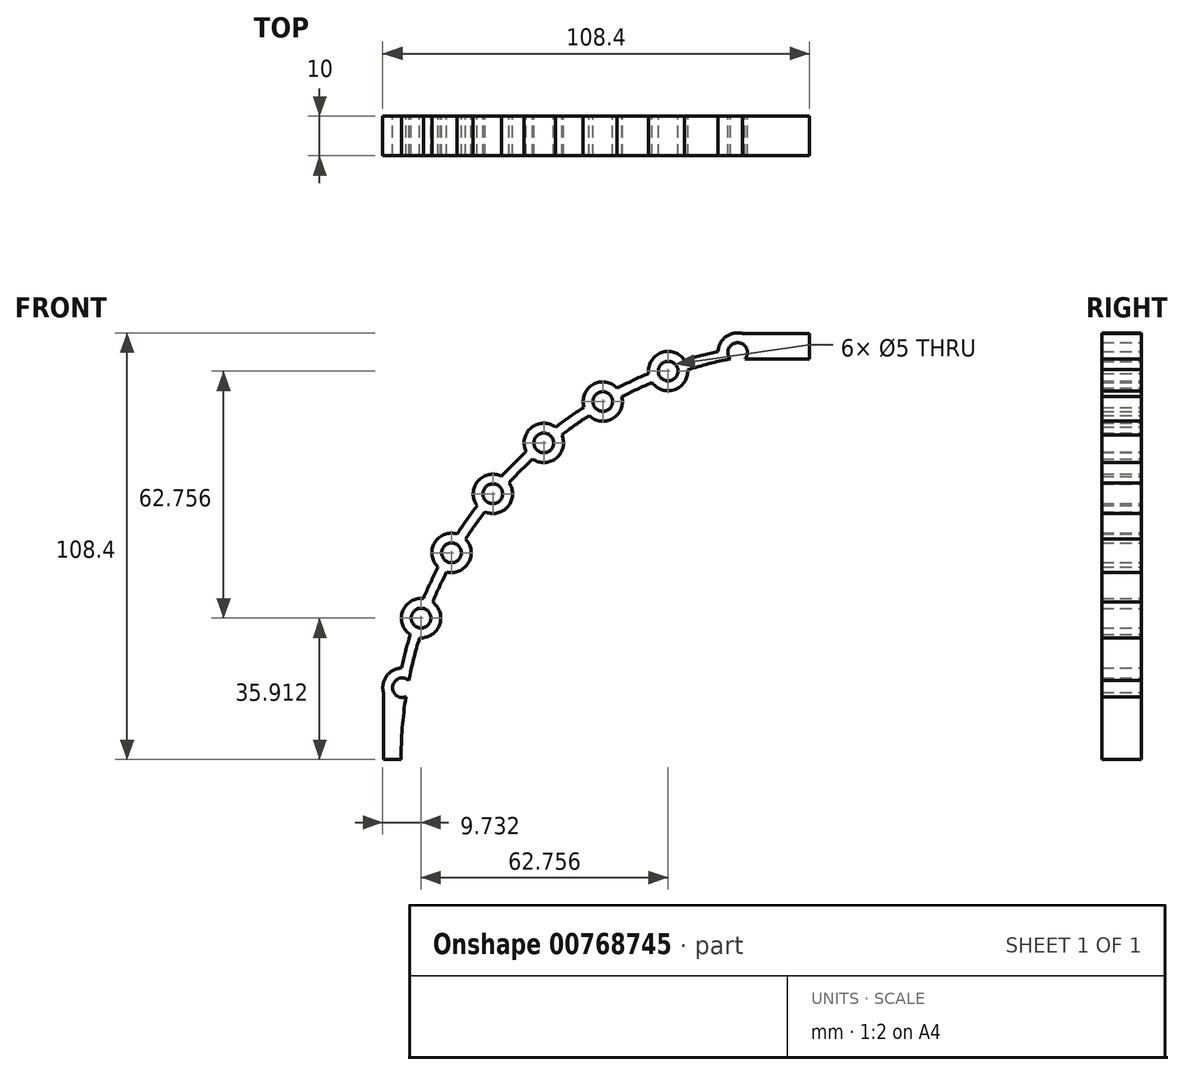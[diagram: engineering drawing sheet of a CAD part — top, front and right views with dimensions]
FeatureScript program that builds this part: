
annotation { "Feature Type Name" : "Feature", "Feature Type Description" : "" }
export const myFeature = defineFeature(function(context is Context, id is Id, definition is map)
    precondition{}
    {
        {
            var Q0;
            Q0=qCreatedBy(makeId("Front.planeOp"),FACE);
            var sketch = newSketch(context, id + "F0", { "sketchPlane" : qUnion([Q0])});
            skCircle(sketch, "E0", {"center": v(0, 0) * mm, "radius": 105 * mm, "construction": true});
            skLineSegment(sketch, "E1", {"start": v(0, 0) * mm, "end": v(0, 105) * mm, "construction": true});
            skLineSegment(sketch, "E2", {"start": v(0, 0) * mm, "end": v(0, -105) * mm, "construction": true});
            skLineSegment(sketch, "E3", {"start": v(0, 0) * mm, "end": v(-105, 0) * mm, "construction": true});
            skLineSegment(sketch, "E4", {"start": v(0, 0) * mm, "end": v(105, 0) * mm, "construction": true});
            skLineSegment(sketch, "E5", {"start": v(0, 0) * mm, "end": v(-18.23, 103.4) * mm, "construction": true});
            skLineSegment(sketch, "E6", {"start": v(0, 0) * mm, "end": v(-35.91, 98.67) * mm, "construction": true});
            skLineSegment(sketch, "E7", {"start": v(0, 0) * mm, "end": v(-52.5, 90.93) * mm, "construction": true});
            skLineSegment(sketch, "E8", {"start": v(0, 0) * mm, "end": v(-67.5, 80.43) * mm, "construction": true});
            skLineSegment(sketch, "E9", {"start": v(0, 0) * mm, "end": v(-80.43, 67.5) * mm, "construction": true});
            skLineSegment(sketch, "E10", {"start": v(0, 0) * mm, "end": v(-90.93, 52.5) * mm, "construction": true});
            skLineSegment(sketch, "E11", {"start": v(0, 0) * mm, "end": v(-98.67, 35.91) * mm, "construction": true});
            skLineSegment(sketch, "E12", {"start": v(0, 0) * mm, "end": v(-103.4, 18.23) * mm, "construction": true});
            skCircle(sketch, "E13", {"center": v(-103.4, 18.23) * mm, "radius": 5 * mm});
            skCircle(sketch, "E14", {"center": v(-98.67, 35.91) * mm, "radius": 5 * mm});
            skCircle(sketch, "E15", {"center": v(-90.93, 52.5) * mm, "radius": 5 * mm});
            skCircle(sketch, "E16", {"center": v(-80.43, 67.5) * mm, "radius": 5 * mm});
            skCircle(sketch, "E17", {"center": v(-67.5, 80.43) * mm, "radius": 5 * mm});
            skCircle(sketch, "E18", {"center": v(-52.5, 90.93) * mm, "radius": 5 * mm});
            skCircle(sketch, "E19", {"center": v(-35.91, 98.67) * mm, "radius": 5 * mm});
            skCircle(sketch, "E20", {"center": v(-18.23, 103.4) * mm, "radius": 5 * mm});
            skCircle(sketch, "E21", {"center": v(0, 0) * mm, "radius": 106.25 * mm});
            skCircle(sketch, "E22", {"center": v(0, 0) * mm, "radius": 103.75 * mm});
            skLineSegment(sketch, "E23.bottom", {"start": v(-101.75, 18) * mm, "end": v(-108.25, 18) * mm});
            skLineSegment(sketch, "E23.top", {"start": v(-101.75, -18) * mm, "end": v(-108.25, -18) * mm});
            skLineSegment(sketch, "E23.left", {"start": v(-101.75, 18) * mm, "end": v(-101.75, -18) * mm});
            skLineSegment(sketch, "E23.right", {"start": v(-108.25, 18) * mm, "end": v(-108.25, -18) * mm});
            skPoint(sketch, "E23.middle", {"position": v(-105, 0) * mm});
            skLineSegment(sketch, "E24", {"start": v(-101.75, 0) * mm, "end": v(-108.25, 0) * mm});
            skLineSegment(sketch, "E25.bottom", {"start": v(-18, 108.25) * mm, "end": v(18, 108.25) * mm});
            skLineSegment(sketch, "E25.top", {"start": v(-18, 101.75) * mm, "end": v(18, 101.75) * mm});
            skLineSegment(sketch, "E25.left", {"start": v(-18, 108.25) * mm, "end": v(-18, 101.75) * mm});
            skLineSegment(sketch, "E25.right", {"start": v(18, 108.25) * mm, "end": v(18, 101.75) * mm});
            skPoint(sketch, "E25.middle", {"position": v(0, 105) * mm});
            skLineSegment(sketch, "E26", {"start": v(0, 101.75) * mm, "end": v(0, 108.25) * mm});
            skSolve(sketch);
        }
        {
            var Q0;
            {var subQ0=sQuery(id+"F0.wireOp",EDGE,"E21");var subQ1=sQuery(id+"F0.wireOp",EDGE,"E13");var subQ2=makeQuery(id+"F0.imprint","INTERSECT",VERTEX,{"disambiguationData":[OD(0.0)],"derivedFrom":[subQ1,subQ0]});Q0=makeQuery(id+"F0.imprint","IMPRINT",FACE,{"disambiguationData":[TD([[makeQuery(id+"F0.imprint","IMPRINT",EDGE,{"disambiguationData":[TD([[subQ2,-1.0]])],"derivedFrom":subQ1}),1.0]])]});}
            var Q1;
            {var subQ0=sQuery(id+"F0.wireOp",EDGE,"E22");var subQ1=sQuery(id+"F0.wireOp",EDGE,"E13");var subQ2=makeQuery(id+"F0.imprint","INTERSECT",VERTEX,{"disambiguationData":[OD(0.0)],"derivedFrom":[subQ1,subQ0]});Q1=makeQuery(id+"F0.imprint","IMPRINT",FACE,{"disambiguationData":[TD([[makeQuery(id+"F0.imprint","IMPRINT",EDGE,{"disambiguationData":[TD([[subQ2,1.0]])],"derivedFrom":subQ1}),1.0]])]});}
            var Q2;
            {var subQ0=sQuery(id+"F0.wireOp",EDGE,"E21");var subQ1=sQuery(id+"F0.wireOp",EDGE,"E13");var subQ2=makeQuery(id+"F0.imprint","INTERSECT",VERTEX,{"disambiguationData":[OD(0.0)],"derivedFrom":[subQ1,subQ0]});Q2=makeQuery(id+"F0.imprint","IMPRINT",FACE,{"disambiguationData":[TD([[makeQuery(id+"F0.imprint","IMPRINT",EDGE,{"disambiguationData":[TD([[subQ2,1.0]])],"derivedFrom":subQ1}),-1.0]])]});}
            var Q3;
            {var subQ0=sQuery(id+"F0.wireOp",EDGE,"E21");var subQ1=sQuery(id+"F0.wireOp",EDGE,"E13");var subQ2=makeQuery(id+"F0.imprint","INTERSECT",VERTEX,{"disambiguationData":[OD(0.0)],"derivedFrom":[subQ1,subQ0]});Q3=makeQuery(id+"F0.imprint","IMPRINT",FACE,{"disambiguationData":[TD([[makeQuery(id+"F0.imprint","IMPRINT",EDGE,{"disambiguationData":[TD([[subQ2,1.0]])],"derivedFrom":subQ1}),1.0]])]});}
            var Q4;
            {var subQ0=sQuery(id+"F0.wireOp",EDGE,"E21");var subQ1=sQuery(id+"F0.wireOp",EDGE,"E14");var subQ2=makeQuery(id+"F0.imprint","INTERSECT",VERTEX,{"disambiguationData":[OD(0.0)],"derivedFrom":[subQ1,subQ0]});Q4=makeQuery(id+"F0.imprint","IMPRINT",FACE,{"disambiguationData":[TD([[makeQuery(id+"F0.imprint","IMPRINT",EDGE,{"disambiguationData":[TD([[subQ2,-1.0]])],"derivedFrom":subQ1}),1.0]])]});}
            var Q5;
            {var subQ0=sQuery(id+"F0.wireOp",EDGE,"E21");var subQ1=sQuery(id+"F0.wireOp",EDGE,"E14");var subQ2=makeQuery(id+"F0.imprint","INTERSECT",VERTEX,{"disambiguationData":[OD(0.0)],"derivedFrom":[subQ1,subQ0]});Q5=makeQuery(id+"F0.imprint","IMPRINT",FACE,{"disambiguationData":[TD([[makeQuery(id+"F0.imprint","IMPRINT",EDGE,{"disambiguationData":[TD([[subQ2,1.0]])],"derivedFrom":subQ1}),1.0]])]});}
            var Q6;
            {var subQ0=sQuery(id+"F0.wireOp",EDGE,"E22");var subQ1=sQuery(id+"F0.wireOp",EDGE,"E14");var subQ2=makeQuery(id+"F0.imprint","INTERSECT",VERTEX,{"disambiguationData":[OD(0.0)],"derivedFrom":[subQ1,subQ0]});Q6=makeQuery(id+"F0.imprint","IMPRINT",FACE,{"disambiguationData":[TD([[makeQuery(id+"F0.imprint","IMPRINT",EDGE,{"disambiguationData":[TD([[subQ2,1.0]])],"derivedFrom":subQ1}),1.0]])]});}
            var Q7;
            {var subQ0=sQuery(id+"F0.wireOp",EDGE,"E21");var subQ1=sQuery(id+"F0.wireOp",EDGE,"E20");var subQ2=makeQuery(id+"F0.imprint","INTERSECT",VERTEX,{"disambiguationData":[OD(0.0)],"derivedFrom":[subQ1,subQ0]});Q7=makeQuery(id+"F0.imprint","IMPRINT",FACE,{"disambiguationData":[TD([[makeQuery(id+"F0.imprint","IMPRINT",EDGE,{"disambiguationData":[TD([[subQ2,1.0]])],"derivedFrom":subQ1}),1.0]])]});}
            var Q8;
            {var subQ0=sQuery(id+"F0.wireOp",EDGE,"E21");var subQ1=sQuery(id+"F0.wireOp",EDGE,"E20");var subQ2=makeQuery(id+"F0.imprint","INTERSECT",VERTEX,{"disambiguationData":[OD(0.0)],"derivedFrom":[subQ1,subQ0]});Q8=makeQuery(id+"F0.imprint","IMPRINT",FACE,{"disambiguationData":[TD([[makeQuery(id+"F0.imprint","IMPRINT",EDGE,{"disambiguationData":[TD([[subQ2,-1.0]])],"derivedFrom":subQ1}),1.0]])]});}
            var Q9;
            {var subQ0=sQuery(id+"F0.wireOp",EDGE,"E22");var subQ1=sQuery(id+"F0.wireOp",EDGE,"E20");var subQ2=makeQuery(id+"F0.imprint","INTERSECT",VERTEX,{"disambiguationData":[OD(0.0)],"derivedFrom":[subQ1,subQ0]});Q9=makeQuery(id+"F0.imprint","IMPRINT",FACE,{"disambiguationData":[TD([[makeQuery(id+"F0.imprint","IMPRINT",EDGE,{"disambiguationData":[TD([[subQ2,-1.0]])],"derivedFrom":subQ1}),1.0]])]});}
            var Q10;
            {var subQ0=sQuery(id+"F0.wireOp",EDGE,"E21");var subQ1=sQuery(id+"F0.wireOp",EDGE,"E19");var subQ2=makeQuery(id+"F0.imprint","INTERSECT",VERTEX,{"disambiguationData":[OD(0.0)],"derivedFrom":[subQ1,subQ0]});Q10=makeQuery(id+"F0.imprint","IMPRINT",FACE,{"disambiguationData":[TD([[makeQuery(id+"F0.imprint","IMPRINT",EDGE,{"disambiguationData":[TD([[subQ2,1.0]])],"derivedFrom":subQ1}),-1.0]])]});}
            var Q11;
            {var subQ0=sQuery(id+"F0.wireOp",EDGE,"E21");var subQ1=sQuery(id+"F0.wireOp",EDGE,"E19");var subQ2=makeQuery(id+"F0.imprint","INTERSECT",VERTEX,{"disambiguationData":[OD(0.0)],"derivedFrom":[subQ1,subQ0]});Q11=makeQuery(id+"F0.imprint","IMPRINT",FACE,{"disambiguationData":[TD([[makeQuery(id+"F0.imprint","IMPRINT",EDGE,{"disambiguationData":[TD([[subQ2,1.0]])],"derivedFrom":subQ1}),1.0]])]});}
            var Q12;
            {var subQ0=sQuery(id+"F0.wireOp",EDGE,"E21");var subQ1=sQuery(id+"F0.wireOp",EDGE,"E19");var subQ2=makeQuery(id+"F0.imprint","INTERSECT",VERTEX,{"disambiguationData":[OD(0.0)],"derivedFrom":[subQ1,subQ0]});Q12=makeQuery(id+"F0.imprint","IMPRINT",FACE,{"disambiguationData":[TD([[makeQuery(id+"F0.imprint","IMPRINT",EDGE,{"disambiguationData":[TD([[subQ2,-1.0]])],"derivedFrom":subQ1}),1.0]])]});}
            var Q13;
            {var subQ0=sQuery(id+"F0.wireOp",EDGE,"E22");var subQ1=sQuery(id+"F0.wireOp",EDGE,"E19");var subQ2=makeQuery(id+"F0.imprint","INTERSECT",VERTEX,{"disambiguationData":[OD(0.0)],"derivedFrom":[subQ1,subQ0]});Q13=makeQuery(id+"F0.imprint","IMPRINT",FACE,{"disambiguationData":[TD([[makeQuery(id+"F0.imprint","IMPRINT",EDGE,{"disambiguationData":[TD([[subQ2,1.0]])],"derivedFrom":subQ1}),1.0]])]});}
            var Q14;
            {var subQ0=sQuery(id+"F0.wireOp",EDGE,"E22");var subQ1=sQuery(id+"F0.wireOp",EDGE,"E18");var subQ2=makeQuery(id+"F0.imprint","INTERSECT",VERTEX,{"disambiguationData":[OD(0.0)],"derivedFrom":[subQ1,subQ0]});Q14=makeQuery(id+"F0.imprint","IMPRINT",FACE,{"disambiguationData":[TD([[makeQuery(id+"F0.imprint","IMPRINT",EDGE,{"disambiguationData":[TD([[subQ2,1.0]])],"derivedFrom":subQ1}),1.0]])]});}
            var Q15;
            {var subQ0=sQuery(id+"F0.wireOp",EDGE,"E21");var subQ1=sQuery(id+"F0.wireOp",EDGE,"E18");var subQ2=makeQuery(id+"F0.imprint","INTERSECT",VERTEX,{"disambiguationData":[OD(0.0)],"derivedFrom":[subQ1,subQ0]});Q15=makeQuery(id+"F0.imprint","IMPRINT",FACE,{"disambiguationData":[TD([[makeQuery(id+"F0.imprint","IMPRINT",EDGE,{"disambiguationData":[TD([[subQ2,1.0]])],"derivedFrom":subQ1}),-1.0]])]});}
            var Q16;
            {var subQ0=sQuery(id+"F0.wireOp",EDGE,"E21");var subQ1=sQuery(id+"F0.wireOp",EDGE,"E18");var subQ2=makeQuery(id+"F0.imprint","INTERSECT",VERTEX,{"disambiguationData":[OD(0.0)],"derivedFrom":[subQ1,subQ0]});Q16=makeQuery(id+"F0.imprint","IMPRINT",FACE,{"disambiguationData":[TD([[makeQuery(id+"F0.imprint","IMPRINT",EDGE,{"disambiguationData":[TD([[subQ2,1.0]])],"derivedFrom":subQ1}),1.0]])]});}
            var Q17;
            {var subQ0=sQuery(id+"F0.wireOp",EDGE,"E21");var subQ1=sQuery(id+"F0.wireOp",EDGE,"E18");var subQ2=makeQuery(id+"F0.imprint","INTERSECT",VERTEX,{"disambiguationData":[OD(0.0)],"derivedFrom":[subQ1,subQ0]});Q17=makeQuery(id+"F0.imprint","IMPRINT",FACE,{"disambiguationData":[TD([[makeQuery(id+"F0.imprint","IMPRINT",EDGE,{"disambiguationData":[TD([[subQ2,-1.0]])],"derivedFrom":subQ1}),1.0]])]});}
            var Q18;
            {var subQ0=sQuery(id+"F0.wireOp",EDGE,"E21");var subQ1=sQuery(id+"F0.wireOp",EDGE,"E17");var subQ2=makeQuery(id+"F0.imprint","INTERSECT",VERTEX,{"disambiguationData":[OD(0.0)],"derivedFrom":[subQ1,subQ0]});Q18=makeQuery(id+"F0.imprint","IMPRINT",FACE,{"disambiguationData":[TD([[makeQuery(id+"F0.imprint","IMPRINT",EDGE,{"disambiguationData":[TD([[subQ2,1.0]])],"derivedFrom":subQ1}),-1.0]])]});}
            var Q19;
            {var subQ0=sQuery(id+"F0.wireOp",EDGE,"E21");var subQ1=sQuery(id+"F0.wireOp",EDGE,"E17");var subQ2=makeQuery(id+"F0.imprint","INTERSECT",VERTEX,{"disambiguationData":[OD(0.0)],"derivedFrom":[subQ1,subQ0]});Q19=makeQuery(id+"F0.imprint","IMPRINT",FACE,{"disambiguationData":[TD([[makeQuery(id+"F0.imprint","IMPRINT",EDGE,{"disambiguationData":[TD([[subQ2,-1.0]])],"derivedFrom":subQ1}),1.0]])]});}
            var Q20;
            {var subQ0=sQuery(id+"F0.wireOp",EDGE,"E22");var subQ1=sQuery(id+"F0.wireOp",EDGE,"E17");var subQ2=makeQuery(id+"F0.imprint","INTERSECT",VERTEX,{"disambiguationData":[OD(0.0)],"derivedFrom":[subQ1,subQ0]});Q20=makeQuery(id+"F0.imprint","IMPRINT",FACE,{"disambiguationData":[TD([[makeQuery(id+"F0.imprint","IMPRINT",EDGE,{"disambiguationData":[TD([[subQ2,1.0]])],"derivedFrom":subQ1}),1.0]])]});}
            var Q21;
            {var subQ0=sQuery(id+"F0.wireOp",EDGE,"E21");var subQ1=sQuery(id+"F0.wireOp",EDGE,"E17");var subQ2=makeQuery(id+"F0.imprint","INTERSECT",VERTEX,{"disambiguationData":[OD(0.0)],"derivedFrom":[subQ1,subQ0]});Q21=makeQuery(id+"F0.imprint","IMPRINT",FACE,{"disambiguationData":[TD([[makeQuery(id+"F0.imprint","IMPRINT",EDGE,{"disambiguationData":[TD([[subQ2,1.0]])],"derivedFrom":subQ1}),1.0]])]});}
            var Q22;
            {var subQ0=sQuery(id+"F0.wireOp",EDGE,"E21");var subQ1=sQuery(id+"F0.wireOp",EDGE,"E16");var subQ2=makeQuery(id+"F0.imprint","INTERSECT",VERTEX,{"disambiguationData":[OD(0.0)],"derivedFrom":[subQ1,subQ0]});Q22=makeQuery(id+"F0.imprint","IMPRINT",FACE,{"disambiguationData":[TD([[makeQuery(id+"F0.imprint","IMPRINT",EDGE,{"disambiguationData":[TD([[subQ2,1.0]])],"derivedFrom":subQ1}),-1.0]])]});}
            var Q23;
            {var subQ0=sQuery(id+"F0.wireOp",EDGE,"E21");var subQ1=sQuery(id+"F0.wireOp",EDGE,"E16");var subQ2=makeQuery(id+"F0.imprint","INTERSECT",VERTEX,{"disambiguationData":[OD(0.0)],"derivedFrom":[subQ1,subQ0]});Q23=makeQuery(id+"F0.imprint","IMPRINT",FACE,{"disambiguationData":[TD([[makeQuery(id+"F0.imprint","IMPRINT",EDGE,{"disambiguationData":[TD([[subQ2,1.0]])],"derivedFrom":subQ1}),1.0]])]});}
            var Q24;
            {var subQ0=sQuery(id+"F0.wireOp",EDGE,"E22");var subQ1=sQuery(id+"F0.wireOp",EDGE,"E16");var subQ2=makeQuery(id+"F0.imprint","INTERSECT",VERTEX,{"disambiguationData":[OD(0.0)],"derivedFrom":[subQ1,subQ0]});Q24=makeQuery(id+"F0.imprint","IMPRINT",FACE,{"disambiguationData":[TD([[makeQuery(id+"F0.imprint","IMPRINT",EDGE,{"disambiguationData":[TD([[subQ2,1.0]])],"derivedFrom":subQ1}),1.0]])]});}
            var Q25;
            {var subQ0=sQuery(id+"F0.wireOp",EDGE,"E21");var subQ1=sQuery(id+"F0.wireOp",EDGE,"E16");var subQ2=makeQuery(id+"F0.imprint","INTERSECT",VERTEX,{"disambiguationData":[OD(0.0)],"derivedFrom":[subQ1,subQ0]});Q25=makeQuery(id+"F0.imprint","IMPRINT",FACE,{"disambiguationData":[TD([[makeQuery(id+"F0.imprint","IMPRINT",EDGE,{"disambiguationData":[TD([[subQ2,-1.0]])],"derivedFrom":subQ1}),1.0]])]});}
            var Q26;
            {var subQ0=sQuery(id+"F0.wireOp",EDGE,"E21");var subQ1=sQuery(id+"F0.wireOp",EDGE,"E15");var subQ2=makeQuery(id+"F0.imprint","INTERSECT",VERTEX,{"disambiguationData":[OD(0.0)],"derivedFrom":[subQ1,subQ0]});Q26=makeQuery(id+"F0.imprint","IMPRINT",FACE,{"disambiguationData":[TD([[makeQuery(id+"F0.imprint","IMPRINT",EDGE,{"disambiguationData":[TD([[subQ2,1.0]])],"derivedFrom":subQ1}),-1.0]])]});}
            var Q27;
            {var subQ0=sQuery(id+"F0.wireOp",EDGE,"E21");var subQ1=sQuery(id+"F0.wireOp",EDGE,"E15");var subQ2=makeQuery(id+"F0.imprint","INTERSECT",VERTEX,{"disambiguationData":[OD(0.0)],"derivedFrom":[subQ1,subQ0]});Q27=makeQuery(id+"F0.imprint","IMPRINT",FACE,{"disambiguationData":[TD([[makeQuery(id+"F0.imprint","IMPRINT",EDGE,{"disambiguationData":[TD([[subQ2,-1.0]])],"derivedFrom":subQ1}),1.0]])]});}
            var Q28;
            {var subQ0=sQuery(id+"F0.wireOp",EDGE,"E21");var subQ1=sQuery(id+"F0.wireOp",EDGE,"E15");var subQ2=makeQuery(id+"F0.imprint","INTERSECT",VERTEX,{"disambiguationData":[OD(0.0)],"derivedFrom":[subQ1,subQ0]});Q28=makeQuery(id+"F0.imprint","IMPRINT",FACE,{"disambiguationData":[TD([[makeQuery(id+"F0.imprint","IMPRINT",EDGE,{"disambiguationData":[TD([[subQ2,1.0]])],"derivedFrom":subQ1}),1.0]])]});}
            var Q29;
            {var subQ0=sQuery(id+"F0.wireOp",EDGE,"E22");var subQ1=sQuery(id+"F0.wireOp",EDGE,"E15");var subQ2=makeQuery(id+"F0.imprint","INTERSECT",VERTEX,{"disambiguationData":[OD(0.0)],"derivedFrom":[subQ1,subQ0]});Q29=makeQuery(id+"F0.imprint","IMPRINT",FACE,{"disambiguationData":[TD([[makeQuery(id+"F0.imprint","IMPRINT",EDGE,{"disambiguationData":[TD([[subQ2,1.0]])],"derivedFrom":subQ1}),1.0]])]});}
            var Q30;
            {var subQ0=sQuery(id+"F0.wireOp",EDGE,"E21");var subQ1=sQuery(id+"F0.wireOp",EDGE,"E14");var subQ2=makeQuery(id+"F0.imprint","INTERSECT",VERTEX,{"disambiguationData":[OD(0.0)],"derivedFrom":[subQ1,subQ0]});Q30=makeQuery(id+"F0.imprint","IMPRINT",FACE,{"disambiguationData":[TD([[makeQuery(id+"F0.imprint","IMPRINT",EDGE,{"disambiguationData":[TD([[subQ2,1.0]])],"derivedFrom":subQ1}),-1.0]])]});}
            var Q31;
            {var subQ0=sQuery(id+"F0.wireOp",EDGE,"E25.bottom");var subQ1=sQuery(id+"F0.wireOp",EDGE,"E20");var subQ2=makeQuery(id+"F0.imprint","INTERSECT",VERTEX,{"derivedFrom":[subQ1,subQ0]});Q31=makeQuery(id+"F0.imprint","IMPRINT",FACE,{"disambiguationData":[TD([[makeQuery(id+"F0.imprint","IMPRINT",EDGE,{"disambiguationData":[TD([[subQ2,1.0]])],"derivedFrom":subQ1}),1.0]])]});}
            var Q32;
            {var subQ0=sQuery(id+"F0.wireOp",EDGE,"E25.bottom");var subQ1=sQuery(id+"F0.wireOp",EDGE,"E20");var subQ2=makeQuery(id+"F0.imprint","INTERSECT",VERTEX,{"derivedFrom":[subQ1,subQ0]});Q32=makeQuery(id+"F0.imprint","IMPRINT",FACE,{"disambiguationData":[TD([[makeQuery(id+"F0.imprint","IMPRINT",EDGE,{"disambiguationData":[TD([[subQ2,1.0]])],"derivedFrom":subQ1}),-1.0]])]});}
            var Q33;
            {var subQ0=sQuery(id+"F0.wireOp",EDGE,"E21");var subQ1=sQuery(id+"F0.wireOp",EDGE,"E20");var subQ2=makeQuery(id+"F0.imprint","INTERSECT",VERTEX,{"disambiguationData":[OD(1.0)],"derivedFrom":[subQ1,subQ0]});Q33=makeQuery(id+"F0.imprint","IMPRINT",FACE,{"disambiguationData":[TD([[makeQuery(id+"F0.imprint","IMPRINT",EDGE,{"disambiguationData":[TD([[subQ2,1.0]])],"derivedFrom":subQ1}),-1.0]])]});}
            var Q34;
            {var subQ0=sQuery(id+"F0.wireOp",EDGE,"E25.top");var subQ1=sQuery(id+"F0.wireOp",EDGE,"E20");var subQ2=makeQuery(id+"F0.imprint","INTERSECT",VERTEX,{"derivedFrom":[subQ1,subQ0]});Q34=makeQuery(id+"F0.imprint","IMPRINT",FACE,{"disambiguationData":[TD([[makeQuery(id+"F0.imprint","IMPRINT",EDGE,{"disambiguationData":[TD([[subQ2,-1.0]])],"derivedFrom":subQ1}),1.0]])]});}
            var Q35;
            {var subQ0=sQuery(id+"F0.wireOp",EDGE,"E21");var subQ1=sQuery(id+"F0.wireOp",EDGE,"E20");var subQ2=makeQuery(id+"F0.imprint","INTERSECT",VERTEX,{"disambiguationData":[OD(1.0)],"derivedFrom":[subQ1,subQ0]});Q35=makeQuery(id+"F0.imprint","IMPRINT",FACE,{"disambiguationData":[TD([[makeQuery(id+"F0.imprint","IMPRINT",EDGE,{"disambiguationData":[TD([[subQ2,1.0]])],"derivedFrom":subQ1}),1.0]])]});}
            var Q36;
            {var subQ0=sQuery(id+"F0.wireOp",EDGE,"E25.top");var subQ1=sQuery(id+"F0.wireOp",EDGE,"E20");var subQ2=makeQuery(id+"F0.imprint","INTERSECT",VERTEX,{"derivedFrom":[subQ1,subQ0]});Q36=makeQuery(id+"F0.imprint","IMPRINT",FACE,{"disambiguationData":[TD([[makeQuery(id+"F0.imprint","IMPRINT",EDGE,{"disambiguationData":[TD([[subQ2,-1.0]])],"derivedFrom":subQ1}),-1.0]])]});}
            var Q37;
            {var subQ0=sQuery(id+"F0.wireOp",EDGE,"E23.right");var subQ1=sQuery(id+"F0.wireOp",EDGE,"E13");var subQ2=makeQuery(id+"F0.imprint","INTERSECT",VERTEX,{"derivedFrom":[subQ1,subQ0]});Q37=makeQuery(id+"F0.imprint","IMPRINT",FACE,{"disambiguationData":[TD([[makeQuery(id+"F0.imprint","IMPRINT",EDGE,{"disambiguationData":[TD([[subQ2,-1.0]])],"derivedFrom":subQ1}),1.0]])]});}
            var Q38;
            {var subQ0=sQuery(id+"F0.wireOp",EDGE,"E21");var subQ1=sQuery(id+"F0.wireOp",EDGE,"E13");var subQ2=makeQuery(id+"F0.imprint","INTERSECT",VERTEX,{"disambiguationData":[OD(1.0)],"derivedFrom":[subQ1,subQ0]});Q38=makeQuery(id+"F0.imprint","IMPRINT",FACE,{"disambiguationData":[TD([[makeQuery(id+"F0.imprint","IMPRINT",EDGE,{"disambiguationData":[TD([[subQ2,-1.0]])],"derivedFrom":subQ1}),1.0]])]});}
            var Q39;
            {var subQ0=sQuery(id+"F0.wireOp",EDGE,"E23.right");var subQ1=sQuery(id+"F0.wireOp",EDGE,"E13");var subQ2=makeQuery(id+"F0.imprint","INTERSECT",VERTEX,{"derivedFrom":[subQ1,subQ0]});Q39=makeQuery(id+"F0.imprint","IMPRINT",FACE,{"disambiguationData":[TD([[makeQuery(id+"F0.imprint","IMPRINT",EDGE,{"disambiguationData":[TD([[subQ2,-1.0]])],"derivedFrom":subQ1}),-1.0]])]});}
            var Q40;
            {var subQ0=sQuery(id+"F0.wireOp",EDGE,"E22");var subQ1=sQuery(id+"F0.wireOp",EDGE,"E13");var subQ2=makeQuery(id+"F0.imprint","INTERSECT",VERTEX,{"disambiguationData":[OD(1.0)],"derivedFrom":[subQ1,subQ0]});Q40=makeQuery(id+"F0.imprint","IMPRINT",FACE,{"disambiguationData":[TD([[makeQuery(id+"F0.imprint","IMPRINT",EDGE,{"disambiguationData":[TD([[subQ2,-1.0]])],"derivedFrom":subQ1}),-1.0]])]});}
            var Q41;
            {var subQ0=sQuery(id+"F0.wireOp",EDGE,"E22");var subQ1=sQuery(id+"F0.wireOp",EDGE,"E13");var subQ2=makeQuery(id+"F0.imprint","INTERSECT",VERTEX,{"disambiguationData":[OD(1.0)],"derivedFrom":[subQ1,subQ0]});Q41=makeQuery(id+"F0.imprint","IMPRINT",FACE,{"disambiguationData":[TD([[makeQuery(id+"F0.imprint","IMPRINT",EDGE,{"disambiguationData":[TD([[subQ2,-1.0]])],"derivedFrom":subQ1}),1.0]])]});}
            var Q42;
            {var subQ0=sQuery(id+"F0.wireOp",EDGE,"E21");var subQ1=sQuery(id+"F0.wireOp",EDGE,"E13");var subQ2=makeQuery(id+"F0.imprint","INTERSECT",VERTEX,{"disambiguationData":[OD(1.0)],"derivedFrom":[subQ1,subQ0]});Q42=makeQuery(id+"F0.imprint","IMPRINT",FACE,{"disambiguationData":[TD([[makeQuery(id+"F0.imprint","IMPRINT",EDGE,{"disambiguationData":[TD([[subQ2,-1.0]])],"derivedFrom":subQ1}),-1.0]])]});}
            var Q43;
            Q43=sQuery(id+"F0.wireOp",EDGE,"E13");
            var Q44;
            Q44=sQuery(id+"F0.wireOp",EDGE,"E14");
            var Q45;
            Q45=sQuery(id+"F0.wireOp",EDGE,"E15");
            var Q46;
            Q46=sQuery(id+"F0.wireOp",EDGE,"E16");
            var Q47;
            Q47=sQuery(id+"F0.wireOp",EDGE,"E17");
            var Q48;
            Q48=sQuery(id+"F0.wireOp",EDGE,"E18");
            var Q49;
            Q49=sQuery(id+"F0.wireOp",EDGE,"E19");
            var Q50;
            Q50=sQuery(id+"F0.wireOp",EDGE,"E20");
            extrude(context, id + "F1", {"entities" : qUnion([Q0, Q1, Q2, Q3, Q4, Q5, Q6, Q7, Q8, Q9, Q10, Q11, Q12, Q13, Q14, Q15, Q16, Q17, Q18, Q19, Q20, Q21, Q22, Q23, Q24, Q25, Q26, Q27, Q28, Q29, Q30, Q31, Q32, Q33, Q34, Q35, Q36, Q37, Q38, Q39, Q40, Q41, Q42]), "surfaceEntities" : qUnion([Q43, Q44, Q45, Q46, Q47, Q48, Q49, Q50]), "depth" : 10 * mm, "offsetDistance" : 25 * mm});
        }
        {
            var Q0;
            Q0=sQuery(id+"F0.wireOp",VERTEX,"E13.center");
            var Q1;
            Q1=sQuery(id+"F0.wireOp",VERTEX,"E11.end");
            var Q2;
            Q2=sQuery(id+"F0.wireOp",VERTEX,"E15.center");
            var Q3;
            Q3=sQuery(id+"F0.wireOp",VERTEX,"E16.center");
            var Q4;
            Q4=sQuery(id+"F0.wireOp",VERTEX,"E17.center");
            var Q5;
            Q5=sQuery(id+"F0.wireOp",VERTEX,"E18.center");
            var Q6;
            Q6=sQuery(id+"F0.wireOp",VERTEX,"E19.center");
            var Q7;
            Q7=sQuery(id+"F0.wireOp",VERTEX,"E5.end");
            var Q8;
            Q8=makeQuery(id+"F1.opExtrude","SWEPT_BODY",BODY,{"disambiguationData":[OSD([sQuery(id+"F0.wireOp",EDGE,"E13"),sQuery(id+"F0.wireOp",EDGE,"E14"),sQuery(id+"F0.wireOp",EDGE,"E15"),sQuery(id+"F0.wireOp",EDGE,"E16"),sQuery(id+"F0.wireOp",EDGE,"E17"),sQuery(id+"F0.wireOp",EDGE,"E18"),sQuery(id+"F0.wireOp",EDGE,"E19"),sQuery(id+"F0.wireOp",EDGE,"E20"),sQuery(id+"F0.wireOp",EDGE,"E21"),sQuery(id+"F0.wireOp",EDGE,"E22")])]});
            hole(context, id + "F2", {"style" : HoleStyle.SIMPLE, "endStyle" : HoleEndStyle.BLIND, "oppositeDirection" : true, "holeDiameter" : 5 * mm, "majorDiameter" : 5 * mm, "holeDepth" : 25 * mm, "isTappedThrough" : true, "tappedDepth" : 12 * mm, "tapClearance" : 3, "startFromSketch" : true, "locations" : qUnion([Q0, Q1, Q2, Q3, Q4, Q5, Q6, Q7]), "scope" : qUnion([Q8])});
        }
        {
            var Q0;
            {var subQ0=sQuery(id+"F0.wireOp",EDGE,"E22");var subQ1=sQuery(id+"F0.wireOp",EDGE,"E13");var subQ2=makeQuery(id+"F0.imprint","INTERSECT",VERTEX,{"disambiguationData":[OD(1.0)],"derivedFrom":[subQ1,subQ0]});Q0=makeQuery(id+"F0.imprint","IMPRINT",FACE,{"disambiguationData":[TD([[makeQuery(id+"F0.imprint","IMPRINT",EDGE,{"disambiguationData":[TD([[subQ2,-1.0]])],"derivedFrom":subQ1}),1.0]])]});}
            var Q1;
            {var subQ0=sQuery(id+"F0.wireOp",EDGE,"E21");var subQ1=sQuery(id+"F0.wireOp",EDGE,"E13");var subQ2=makeQuery(id+"F0.imprint","INTERSECT",VERTEX,{"disambiguationData":[OD(1.0)],"derivedFrom":[subQ1,subQ0]});Q1=makeQuery(id+"F0.imprint","IMPRINT",FACE,{"disambiguationData":[TD([[makeQuery(id+"F0.imprint","IMPRINT",EDGE,{"disambiguationData":[TD([[subQ2,-1.0]])],"derivedFrom":subQ1}),1.0]])]});}
            var Q2;
            {var subQ0=sQuery(id+"F0.wireOp",EDGE,"E23.right");var subQ1=sQuery(id+"F0.wireOp",EDGE,"E13");var subQ2=makeQuery(id+"F0.imprint","INTERSECT",VERTEX,{"derivedFrom":[subQ1,subQ0]});Q2=makeQuery(id+"F0.imprint","IMPRINT",FACE,{"disambiguationData":[TD([[makeQuery(id+"F0.imprint","IMPRINT",EDGE,{"disambiguationData":[TD([[subQ2,-1.0]])],"derivedFrom":subQ1}),1.0]])]});}
            var Q3;
            {var subQ0=sQuery(id+"F0.wireOp",EDGE,"E23.right");var subQ1=sQuery(id+"F0.wireOp",EDGE,"E13");var subQ2=makeQuery(id+"F0.imprint","INTERSECT",VERTEX,{"derivedFrom":[subQ1,subQ0]});Q3=makeQuery(id+"F0.imprint","IMPRINT",FACE,{"disambiguationData":[TD([[makeQuery(id+"F0.imprint","IMPRINT",EDGE,{"disambiguationData":[TD([[subQ2,-1.0]])],"derivedFrom":subQ1}),-1.0]])]});}
            var Q4;
            {var subQ0=sQuery(id+"F0.wireOp",EDGE,"E21");var subQ1=sQuery(id+"F0.wireOp",EDGE,"E13");var subQ2=makeQuery(id+"F0.imprint","INTERSECT",VERTEX,{"disambiguationData":[OD(1.0)],"derivedFrom":[subQ1,subQ0]});Q4=makeQuery(id+"F0.imprint","IMPRINT",FACE,{"disambiguationData":[TD([[makeQuery(id+"F0.imprint","IMPRINT",EDGE,{"disambiguationData":[TD([[subQ2,-1.0]])],"derivedFrom":subQ1}),-1.0]])]});}
            var Q5;
            {var subQ0=sQuery(id+"F0.wireOp",EDGE,"E22");var subQ1=sQuery(id+"F0.wireOp",EDGE,"E13");var subQ2=makeQuery(id+"F0.imprint","INTERSECT",VERTEX,{"disambiguationData":[OD(1.0)],"derivedFrom":[subQ1,subQ0]});Q5=makeQuery(id+"F0.imprint","IMPRINT",FACE,{"disambiguationData":[TD([[makeQuery(id+"F0.imprint","IMPRINT",EDGE,{"disambiguationData":[TD([[subQ2,-1.0]])],"derivedFrom":subQ1}),-1.0]])]});}
            extrude(context, id + "F3", {"entities" : qUnion([Q0, Q1, Q2, Q3, Q4, Q5]), "operationType" : NewBodyOperationType.ADD, "depth" : 10 * mm, "offsetDistance" : 25 * mm});
        }
        {
            var Q0;
            Q0=sQuery(id+"F0.wireOp",VERTEX,"E12.end");
            var Q1;
            Q1=makeQuery(id+"F1.opExtrude","SWEPT_BODY",BODY,{"disambiguationData":[OSD([sQuery(id+"F0.wireOp",EDGE,"E13"),sQuery(id+"F0.wireOp",EDGE,"E14"),sQuery(id+"F0.wireOp",EDGE,"E15"),sQuery(id+"F0.wireOp",EDGE,"E16"),sQuery(id+"F0.wireOp",EDGE,"E17"),sQuery(id+"F0.wireOp",EDGE,"E18"),sQuery(id+"F0.wireOp",EDGE,"E19"),sQuery(id+"F0.wireOp",EDGE,"E20"),sQuery(id+"F0.wireOp",EDGE,"E21"),sQuery(id+"F0.wireOp",EDGE,"E22"),sQuery(id+"F0.wireOp",EDGE,"E23.bottom"),sQuery(id+"F0.wireOp",EDGE,"E23.left"),sQuery(id+"F0.wireOp",EDGE,"E23.right")])]});
            hole(context, id + "F4", {"style" : HoleStyle.SIMPLE, "endStyle" : HoleEndStyle.BLIND, "oppositeDirection" : true, "holeDiameter" : 5 * mm, "majorDiameter" : 5 * mm, "holeDepth" : 25 * mm, "isTappedThrough" : true, "tappedDepth" : 12 * mm, "tapClearance" : 3, "startFromSketch" : true, "locations" : qUnion([Q0]), "scope" : qUnion([Q1])});
        }
    });
